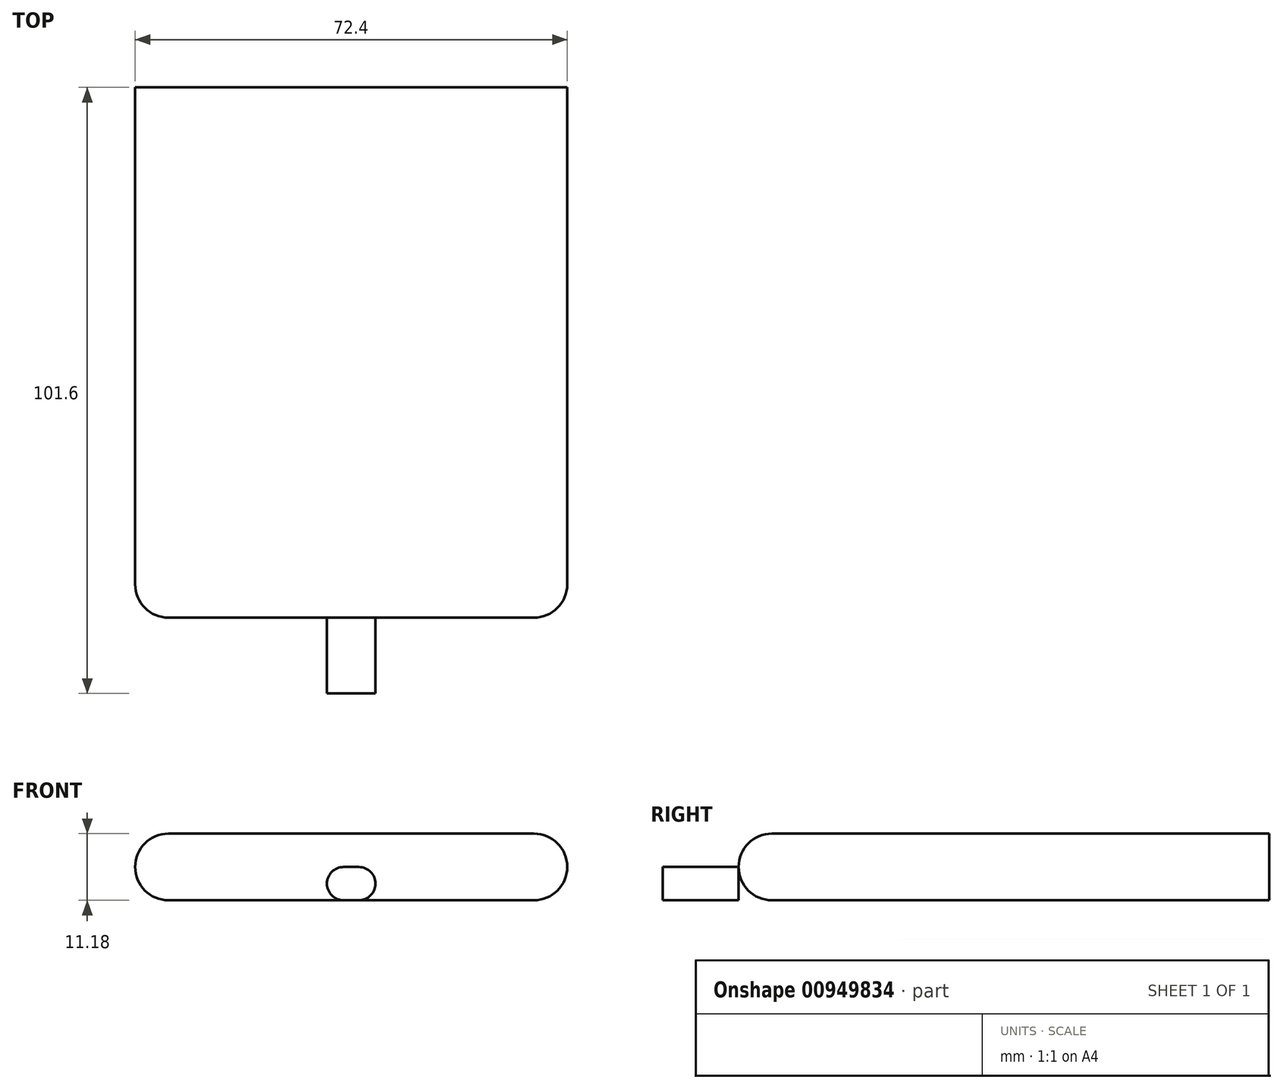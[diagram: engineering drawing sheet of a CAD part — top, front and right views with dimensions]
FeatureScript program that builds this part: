
annotation { "Feature Type Name" : "Feature", "Feature Type Description" : "" }
export const myFeature = defineFeature(function(context is Context, id is Id, definition is map)
    precondition{}
    {
        {
            var Q0;
            Q0=qCreatedBy(makeId("Front.planeOp"),FACE);
            var sketch = newSketch(context, id + "F0", { "sketchPlane" : qUnion([Q0])});
            skLineSegment(sketch, "E0", {"start": v(0, 0) * mm, "end": v(0, -11.18) * mm});
            skLineSegment(sketch, "E1.bottom", {"start": v(36.2, 0) * mm, "end": v(-36.2, 0) * mm});
            skLineSegment(sketch, "E1.top", {"start": v(36.2, -11.18) * mm, "end": v(-36.2, -11.18) * mm});
            skLineSegment(sketch, "E1.left", {"start": v(36.2, 0) * mm, "end": v(36.2, -11.18) * mm});
            skLineSegment(sketch, "E1.right", {"start": v(-36.2, 0) * mm, "end": v(-36.2, -11.18) * mm});
            skPoint(sketch, "E1.middle", {"position": v(0, -5.59) * mm});
            skLineSegment(sketch, "E2", {"start": v(-36.2, -5.59) * mm, "end": v(-30.6, -5.59) * mm});
            skCircle(sketch, "E3", {"center": v(-30.6, -5.59) * mm, "radius": 5.59 * mm});
            skLineSegment(sketch, "E4", {"start": v(36.2, -5.59) * mm, "end": v(30.6, -5.59) * mm});
            skCircle(sketch, "E5", {"center": v(30.6, -5.59) * mm, "radius": 5.59 * mm});
            skSolve(sketch);
        }
        {
            var Q0;
            {var subQ0=sQuery(id+"F0.wireOp",EDGE,"E3");var subQ1=makeQuery(id+"F0.imprint","INTERSECT",VERTEX,{"derivedFrom":[sQuery(id+"F0.wireOp",EDGE,"E1.right"),subQ0]});Q0=makeQuery(id+"F0.imprint","IMPRINT",FACE,{"disambiguationData":[TD([[makeQuery(id+"F0.imprint","IMPRINT",EDGE,{"disambiguationData":[TD([[subQ1,1.0]])],"derivedFrom":subQ0}),1.0]])]});}
            var Q1;
            {var subQ0=sQuery(id+"F0.wireOp",EDGE,"E0");Q1=makeQuery(id+"F0.imprint","IMPRINT",FACE,{"disambiguationData":[TD([[makeQuery(id+"F0.imprint","IMPRINT",EDGE,{"derivedFrom":subQ0}),-1.0]])]});}
            var Q2;
            {var subQ0=sQuery(id+"F0.wireOp",EDGE,"E0");Q2=makeQuery(id+"F0.imprint","IMPRINT",FACE,{"disambiguationData":[TD([[makeQuery(id+"F0.imprint","IMPRINT",EDGE,{"derivedFrom":subQ0}),1.0]])]});}
            var Q3;
            {var subQ0=sQuery(id+"F0.wireOp",EDGE,"E5");var subQ1=makeQuery(id+"F0.imprint","INTERSECT",VERTEX,{"derivedFrom":[sQuery(id+"F0.wireOp",EDGE,"E1.left"),subQ0]});Q3=makeQuery(id+"F0.imprint","IMPRINT",FACE,{"disambiguationData":[TD([[makeQuery(id+"F0.imprint","IMPRINT",EDGE,{"disambiguationData":[TD([[subQ1,-1.0]])],"derivedFrom":subQ0}),1.0]])]});}
            extrude(context, id + "F1", {"entities" : qUnion([Q0, Q1, Q2, Q3]), "depth" : 88.9 * mm, "offsetDistance" : 25.4 * mm});
        }
        {
            var Q0;
            Q0=makeQuery(id+"F1.opExtrude","CAP_FACE",FACE,{"disambiguationData":[OSD([sQuery(id+"F0.wireOp",EDGE,"E1.bottom"),sQuery(id+"F0.wireOp",EDGE,"E1.top"),sQuery(id+"F0.wireOp",EDGE,"E3"),sQuery(id+"F0.wireOp",EDGE,"E5")])],"isStart":false});
            var sketch = newSketch(context, id + "F2", { "sketchPlane" : qUnion([Q0])});
            skLineSegment(sketch, "E6", {"start": v(-36.2, -5.59) * mm, "end": v(36.2, -5.59) * mm});
            skLineSegment(sketch, "E7", {"start": v(0, -5.59) * mm, "end": v(0, -11.18) * mm});
            skLineSegment(sketch, "E8", {"start": v(0, -8.38) * mm, "end": v(4.06, -8.38) * mm});
            skLineSegment(sketch, "E9", {"start": v(0, -8.38) * mm, "end": v(-4.06, -8.38) * mm});
            skLineSegment(sketch, "E10", {"start": v(-4.06, -8.38) * mm, "end": v(-1.27, -8.38) * mm});
            skLineSegment(sketch, "E11", {"start": v(4.06, -8.38) * mm, "end": v(1.27, -8.38) * mm});
            skCircle(sketch, "E12", {"center": v(-1.27, -8.38) * mm, "radius": 2.8 * mm});
            skLineSegment(sketch, "E13", {"start": v(-1.27, -5.59) * mm, "end": v(4.06, -5.59) * mm});
            skLineSegment(sketch, "E14", {"start": v(-1.27, -11.18) * mm, "end": v(4.06, -11.18) * mm});
            skCircle(sketch, "E15", {"center": v(1.27, -8.38) * mm, "radius": 2.8 * mm});
            skLineSegment(sketch, "E16", {"start": v(-1.27, -5.59) * mm, "end": v(1.27, -5.59) * mm});
            skLineSegment(sketch, "E17", {"start": v(-1.27, -11.18) * mm, "end": v(1.27, -11.18) * mm});
            skSolve(sketch);
        }
        {
            var Q0;
            Q0=makeQuery(id+"F1.opExtrude","CAP_EDGE",EDGE,{"disambiguationData":[OSD([sQuery(id+"F0.wireOp",EDGE,"E1.bottom")])],"isStart":false});
            fillet(context, id + "F3", {"entities" : qUnion([Q0]), "radius" : 5.6 * mm, "tangentPropagation" : true, "allowEdgeOverflow" : false});
        }
        {
            var Q0;
            {var subQ0=sQuery(id+"F2.wireOp",EDGE,"E12");var subQ1=sQuery(id+"F2.wireOp",EDGE,"E8");var subQ2=makeQuery(id+"F2.imprint","INTERSECT",VERTEX,{"derivedFrom":[subQ1,subQ0]});Q0=makeQuery(id+"F2.imprint","IMPRINT",FACE,{"disambiguationData":[TD([[makeQuery(id+"F2.imprint","IMPRINT",EDGE,{"disambiguationData":[TD([[subQ2,-1.0]])],"derivedFrom":subQ1}),1.0]])]});}
            var Q1;
            {var subQ0=sQuery(id+"F2.wireOp",EDGE,"E7");var subQ1=sQuery(id+"F2.wireOp",EDGE,"E6");var subQ2=makeQuery(id+"F2.imprint","INTERSECT",VERTEX,{"derivedFrom":[subQ1,subQ0]});Q1=makeQuery(id+"F2.imprint","IMPRINT",FACE,{"disambiguationData":[TD([[makeQuery(id+"F2.imprint","IMPRINT",EDGE,{"disambiguationData":[TD([[subQ2,1.0]])],"derivedFrom":subQ1}),-1.0]])]});}
            var Q2;
            {var subQ0=sQuery(id+"F2.wireOp",EDGE,"E15");var subQ1=sQuery(id+"F2.wireOp",EDGE,"E9");var subQ2=makeQuery(id+"F2.imprint","INTERSECT",VERTEX,{"derivedFrom":[subQ1,subQ0]});Q2=makeQuery(id+"F2.imprint","IMPRINT",FACE,{"disambiguationData":[TD([[makeQuery(id+"F2.imprint","IMPRINT",EDGE,{"disambiguationData":[TD([[subQ2,-1.0]])],"derivedFrom":subQ1}),-1.0]])]});}
            var Q3;
            {var subQ0=sQuery(id+"F2.wireOp",EDGE,"E8");var subQ6=makeQuery(id+"F2.imprint","IMPRINT",VERTEX,{"derivedFrom":subQ0});Q3=makeQuery(id+"F2.imprint","IMPRINT",FACE,{"disambiguationData":[TD([[makeQuery(id+"F2.imprint","IMPRINT",EDGE,{"disambiguationData":[TD([[subQ6,-1.0]])],"derivedFrom":subQ0}),1.0]])]});}
            var Q4;
            {var subQ0=sQuery(id+"F2.wireOp",EDGE,"E9");var subQ5=makeQuery(id+"F2.imprint","IMPRINT",VERTEX,{"derivedFrom":subQ0});Q4=makeQuery(id+"F2.imprint","IMPRINT",FACE,{"disambiguationData":[TD([[makeQuery(id+"F2.imprint","IMPRINT",EDGE,{"disambiguationData":[TD([[subQ5,-1.0]])],"derivedFrom":subQ0}),-1.0]])]});}
            var Q5;
            {var subQ0=sQuery(id+"F2.wireOp",EDGE,"E9");var subQ5=makeQuery(id+"F2.imprint","IMPRINT",VERTEX,{"derivedFrom":subQ0});Q5=makeQuery(id+"F2.imprint","IMPRINT",FACE,{"disambiguationData":[TD([[makeQuery(id+"F2.imprint","IMPRINT",EDGE,{"disambiguationData":[TD([[subQ5,-1.0]])],"derivedFrom":subQ0}),1.0]])]});}
            var Q6;
            {var subQ0=sQuery(id+"F2.wireOp",EDGE,"E8");var subQ5=makeQuery(id+"F2.imprint","IMPRINT",VERTEX,{"derivedFrom":subQ0});Q6=makeQuery(id+"F2.imprint","IMPRINT",FACE,{"disambiguationData":[TD([[makeQuery(id+"F2.imprint","IMPRINT",EDGE,{"disambiguationData":[TD([[subQ5,-1.0]])],"derivedFrom":subQ0}),-1.0]])]});}
            var Q7;
            {var subQ0=sQuery(id+"F2.wireOp",EDGE,"E12");var subQ1=sQuery(id+"F2.wireOp",EDGE,"E8");var subQ2=makeQuery(id+"F2.imprint","INTERSECT",VERTEX,{"derivedFrom":[subQ1,subQ0]});Q7=makeQuery(id+"F2.imprint","IMPRINT",FACE,{"disambiguationData":[TD([[makeQuery(id+"F2.imprint","IMPRINT",EDGE,{"disambiguationData":[TD([[subQ2,-1.0]])],"derivedFrom":subQ1}),-1.0]])]});}
            var Q8;
            {var subQ0=sQuery(id+"F2.wireOp",EDGE,"E15");var subQ1=sQuery(id+"F2.wireOp",EDGE,"E9");var subQ2=makeQuery(id+"F2.imprint","INTERSECT",VERTEX,{"derivedFrom":[subQ1,subQ0]});Q8=makeQuery(id+"F2.imprint","IMPRINT",FACE,{"disambiguationData":[TD([[makeQuery(id+"F2.imprint","IMPRINT",EDGE,{"disambiguationData":[TD([[subQ2,-1.0]])],"derivedFrom":subQ1}),1.0]])]});}
            var Q9;
            {var subQ0=sQuery(id+"F2.wireOp",EDGE,"E7");var subQ1=sQuery(id+"F2.wireOp",EDGE,"E6");var subQ2=makeQuery(id+"F2.imprint","INTERSECT",VERTEX,{"derivedFrom":[subQ1,subQ0]});Q9=makeQuery(id+"F2.imprint","IMPRINT",FACE,{"disambiguationData":[TD([[makeQuery(id+"F2.imprint","IMPRINT",EDGE,{"disambiguationData":[TD([[subQ2,-1.0]])],"derivedFrom":subQ1}),-1.0]])]});}
            var Q10;
            {var subQ0=sQuery(id+"F2.wireOp",EDGE,"E14");var subQ1=sQuery(id+"F2.wireOp",EDGE,"E7");var subQ2=makeQuery(id+"F2.imprint","INTERSECT",VERTEX,{"derivedFrom":[subQ1,subQ0]});Q10=makeQuery(id+"F2.imprint","IMPRINT",FACE,{"disambiguationData":[TD([[makeQuery(id+"F2.imprint","IMPRINT",EDGE,{"disambiguationData":[TD([[subQ2,1.0]])],"derivedFrom":subQ0}),-1.0]])]});}
            var Q11;
            {var subQ0=sQuery(id+"F2.wireOp",EDGE,"E14");var subQ1=sQuery(id+"F2.wireOp",EDGE,"E7");var subQ2=makeQuery(id+"F2.imprint","INTERSECT",VERTEX,{"derivedFrom":[subQ1,subQ0]});Q11=makeQuery(id+"F2.imprint","IMPRINT",FACE,{"disambiguationData":[TD([[makeQuery(id+"F2.imprint","IMPRINT",EDGE,{"disambiguationData":[TD([[subQ2,1.0]])],"derivedFrom":subQ1}),-1.0]])]});}
            extrude(context, id + "F4", {"entities" : qUnion([Q0, Q1, Q2, Q3, Q4, Q5, Q6, Q7, Q8, Q9, Q10, Q11]), "depth" : 12.7 * mm, "offsetDistance" : 25.4 * mm});
        }
    });
